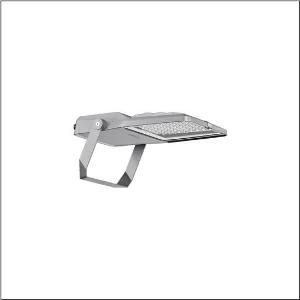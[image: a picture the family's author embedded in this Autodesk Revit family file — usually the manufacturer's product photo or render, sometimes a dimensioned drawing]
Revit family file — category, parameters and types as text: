
# Revit family: floodlight_fl_21_iq_mini___pl43_5xa7771d4a1a_5f3b
name_source: partatom
category: Lighting Fixtures
units: mm (PartAtom-declared; Revit-internal decimal feet)

## family parameters
Cut with Voids When Loaded = No
Host = Face
Light Source = No
Part Type = Normal
Room Calculation Point = No
Round Connector Dimension = Use Diameter
Shared = No

## types (1)
- --- (1 x LED, 19090 lm, 143 W, 4000K)
    Apparent Load = 143 VA
    CIE Flux Codes = 27 78 99 100 100
    Color Rendering = 70
    Color Temperature = 4000K
    Default Elevation = 1800 mm
    Description = Floodlight FL 21 iQ mini, floodlight, primary light control with lens, of PMMA, primary optical cover: protective disc, of toughened safety glass, transparent, light distribution: PL43, light emission: direct distribution, installation type: surface-mounted, LED, High Power LED, rated luminous flux: 19.090lm, luminous efficacy: 134lm/W, light colour: 740, colour temperature: 4000K, control: Auto-Match, Temp-Guard, Lumen-Switch, Night-Set, Smart-Wire, Light-Fading, Desk-Remote (wireless, voltage-free reading and setting of iQ features in the workshop via application-optimized NFC function/RFID function), optimised constant luminous flux control (CLO 2.0), with terminal, 6-pole, mains connection: 220..240V, AC, 50/60Hz, start of lifetime: 143W, end of service life: 152W, reduction: 61W, luminaire housing, of diecast aluminium, powder-coated, Siteco® metallic grey (DB 702S), corrosivity category C5 mid according to DIN EN ISO 12944, sealing non-destructively replaceable, mounting bracket, of steel, galvanised, powder-coated, Siteco® metallic grey (DB 702S), protection rating (complete): IP66, insulation class (complete): insulation class II (safety insulation), certification: CE, ENEC, VDE, protection symbol: D, impact resistance: IK08, permissible operating ambient temperature: -40..+40°C, permissible operating ambient temperature for outdoor applications: -40..+50°C, standard: DIN EN 12944, LABS conformity tested according to VDMA 24364:2018-05, packaging unit: 1 piece

Light Distribution: PL43
    Height = 70 mm
    Lamp = 1 x LED
    Lamp Light Flux = 19090 lm
    Lamp Power = 143 W
    Lamp count = 1
    Length = 485 mm
    Luminous efficacy = 133 lm/W
    Manufacturer = Siteco
    ModVariant = No
    Model = 5XA7771D4A1A
    Number of Poles = 1
    OnlyDefault = Yes
    Power Factor = 1
    Product Name = Floodlight FL 21 iQ mini | PL43
    Product group = floodlight | pylon annexe
    ProductGroupID = 6200
    Protection Class = Protection class II
    Protection Degree = IP 66
    RLX_Detail_Level = 1
    RLX_Emergency_Light_Flux = 0 lm
    RLX_Emergency_Type = 0
    RLX_Emergency_Type_DB = No
    RlxData = <blob elided: 96585 chars, md5=d9cd2377>
    Socket = socket
    Standby Power = 0 W
    System Light Flux = 19090 lm
    System Power = 143 W
    Type Comments = factory setting: luminous flux: 100 % | dim-lin: 254 | 730 mA
    Type Image = l_1006845.jpg
    URL = http://relux.com
    VarID = @adj_111549
    Voltage = 0 V
    Weight = 0.00 kg
    Width = 337 mm

## geometry (parser evidence)
native form markers: Blend x4, Sweep x12
no freeform markers — native parametric forms only
